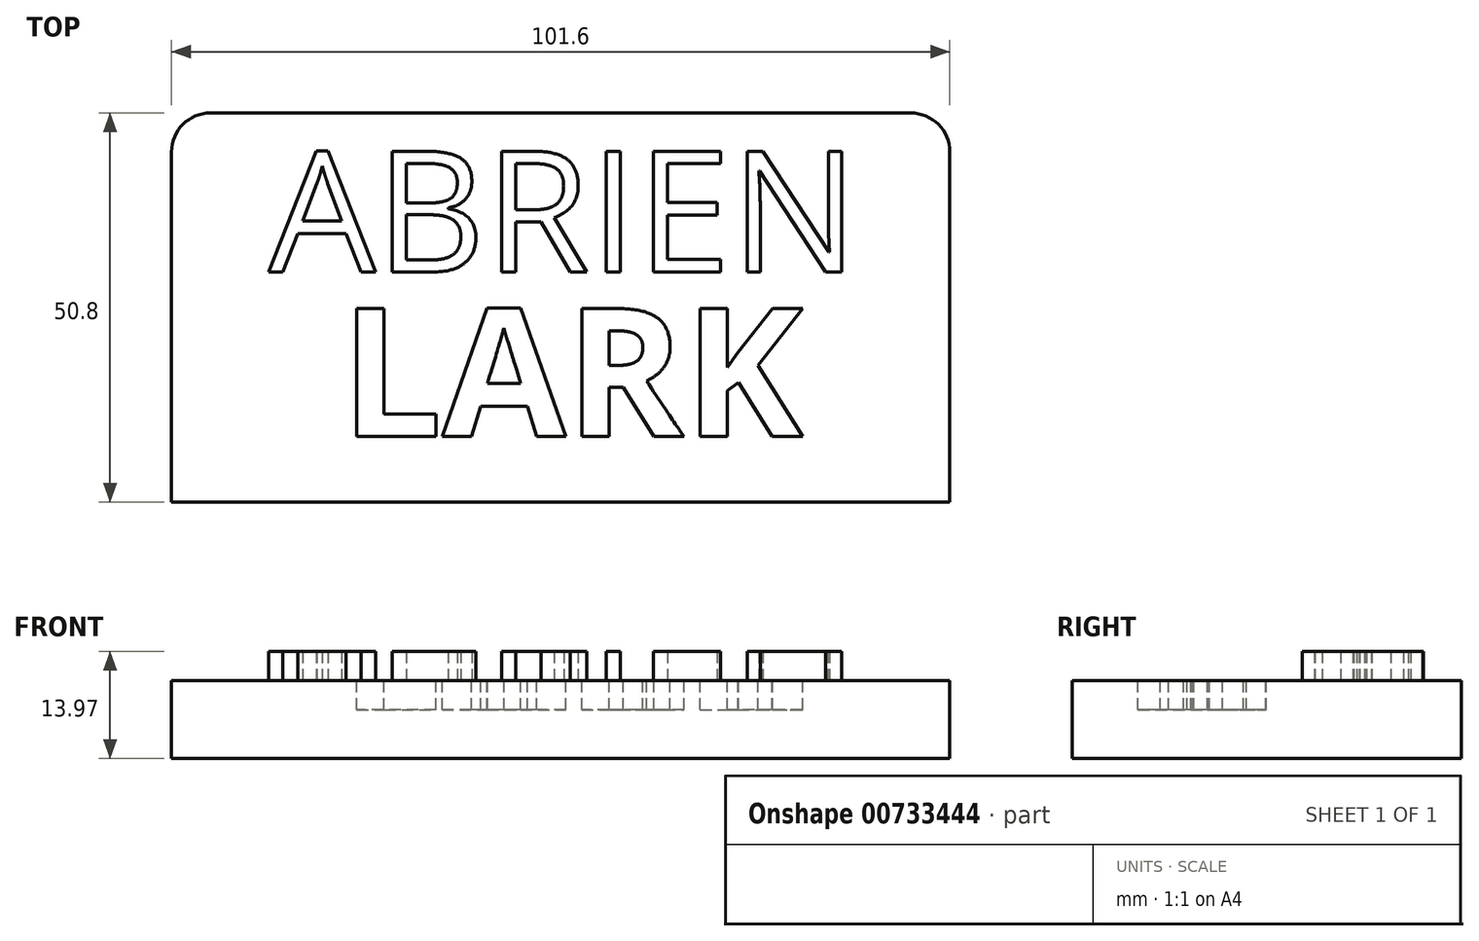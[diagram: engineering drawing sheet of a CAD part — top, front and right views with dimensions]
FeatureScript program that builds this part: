
annotation { "Feature Type Name" : "Feature", "Feature Type Description" : "" }
export const myFeature = defineFeature(function(context is Context, id is Id, definition is map)
    precondition{}
    {
        {
            var Q0;
            Q0=qCreatedBy(makeId("Top.planeOp"),FACE);
            var sketch = newSketch(context, id + "F0", { "sketchPlane" : qUnion([Q0])});
            skLineSegment(sketch, "E0.bottom", {"start": v(50.8, -25.4) * mm, "end": v(-50.8, -25.4) * mm});
            skLineSegment(sketch, "E0.top", {"start": v(50.8, 25.4) * mm, "end": v(-50.8, 25.4) * mm});
            skLineSegment(sketch, "E0.left", {"start": v(50.8, -25.4) * mm, "end": v(50.8, 25.4) * mm});
            skLineSegment(sketch, "E0.right", {"start": v(-50.8, -25.4) * mm, "end": v(-50.8, 25.4) * mm});
            skPoint(sketch, "E0.middle", {"position": v(0, 0) * mm});
            skSolve(sketch);
        }
        {
            var Q0;
            Q0 = qSketchRegion(id + "F0", true);
            extrude(context, id + "F1", {"entities" : qUnion([Q0]), "depth" : 10.16 * mm, "offsetDistance" : 25.4 * mm});
        }
        {
            var Q0;
            Q0=makeQuery(id+"F1.opExtrude","CAP_FACE",FACE,{"disambiguationData":[OSD([sQuery(id+"F0.wireOp",EDGE,"E0.bottom"),sQuery(id+"F0.wireOp",EDGE,"E0.top"),sQuery(id+"F0.wireOp",EDGE,"E0.left"),sQuery(id+"F0.wireOp",EDGE,"E0.right")])],"isStart":false});
            var sketch = newSketch(context, id + "F2", { "sketchPlane" : qUnion([Q0])});
            skText(sketch, "E1", { "text": "ABRIEN", "fontName": "OpenSans-Regular.ttf"});
            const initialGuessF2  = {"E1": [-0.0381, 0.00465, 1, 0, 0.01588]};
            skSetInitialGuess(sketch, initialGuessF2);
            skSolve(sketch);
        }
        {
            var Q0;
            Q0=makeQuery(id+"F1.opExtrude","CAP_FACE",FACE,{"disambiguationData":[OSD([sQuery(id+"F0.wireOp",EDGE,"E0.bottom"),sQuery(id+"F0.wireOp",EDGE,"E0.top"),sQuery(id+"F0.wireOp",EDGE,"E0.left"),sQuery(id+"F0.wireOp",EDGE,"E0.right")])],"isStart":false});
            var sketch = newSketch(context, id + "F3", { "sketchPlane" : qUnion([Q0])});
            skText(sketch, "E2", { "text": "LARK", "fontName": "OpenSans-Bold.ttf"});
            const initialGuessF3  = {"E2": [-0.02869, -0.01684, 1, 0, 0.01684]};
            skSetInitialGuess(sketch, initialGuessF3);
            skSolve(sketch);
        }
        {
            var Q0;
            Q0 = qSketchRegion(id + "F3", true);
            extrude(context, id + "F4", {"entities" : qUnion([Q0]), "operationType" : NewBodyOperationType.REMOVE, "oppositeDirection" : true, "depth" : 3.8 * mm, "offsetDistance" : 25.4 * mm});
        }
        {
            var Q0;
            Q0 = qSketchRegion(id + "F2", true);
            extrude(context, id + "F5", {"entities" : qUnion([Q0]), "operationType" : NewBodyOperationType.ADD, "depth" : 3.8 * mm, "offsetDistance" : 25.4 * mm});
        }
        {
            var Q0;
            Q0=makeQuery(id+"F1.opExtrude","SWEPT_EDGE",EDGE,{"disambiguationData":[OSD([sQuery(id+"F0.wireOp",EDGE,"E0.top"),sQuery(id+"F0.wireOp",EDGE,"E0.right")])]});
            fillet(context, id + "F6", {"entities" : qUnion([Q0]), "tangentPropagation" : true, "radius" : 5.08 * mm, "defaultsChanged" : false, "vertexSettings" : [], "allowEdgeOverflow" : false});
        }
        {
            var Q0;
            Q0=makeQuery(id+"F1.opExtrude","SWEPT_EDGE",EDGE,{"disambiguationData":[OSD([sQuery(id+"F0.wireOp",EDGE,"E0.top"),sQuery(id+"F0.wireOp",EDGE,"E0.left")])]});
            fillet(context, id + "F7", {"entities" : qUnion([Q0]), "tangentPropagation" : true, "radius" : 5.08 * mm, "defaultsChanged" : false, "vertexSettings" : [], "allowEdgeOverflow" : false});
        }
    });
